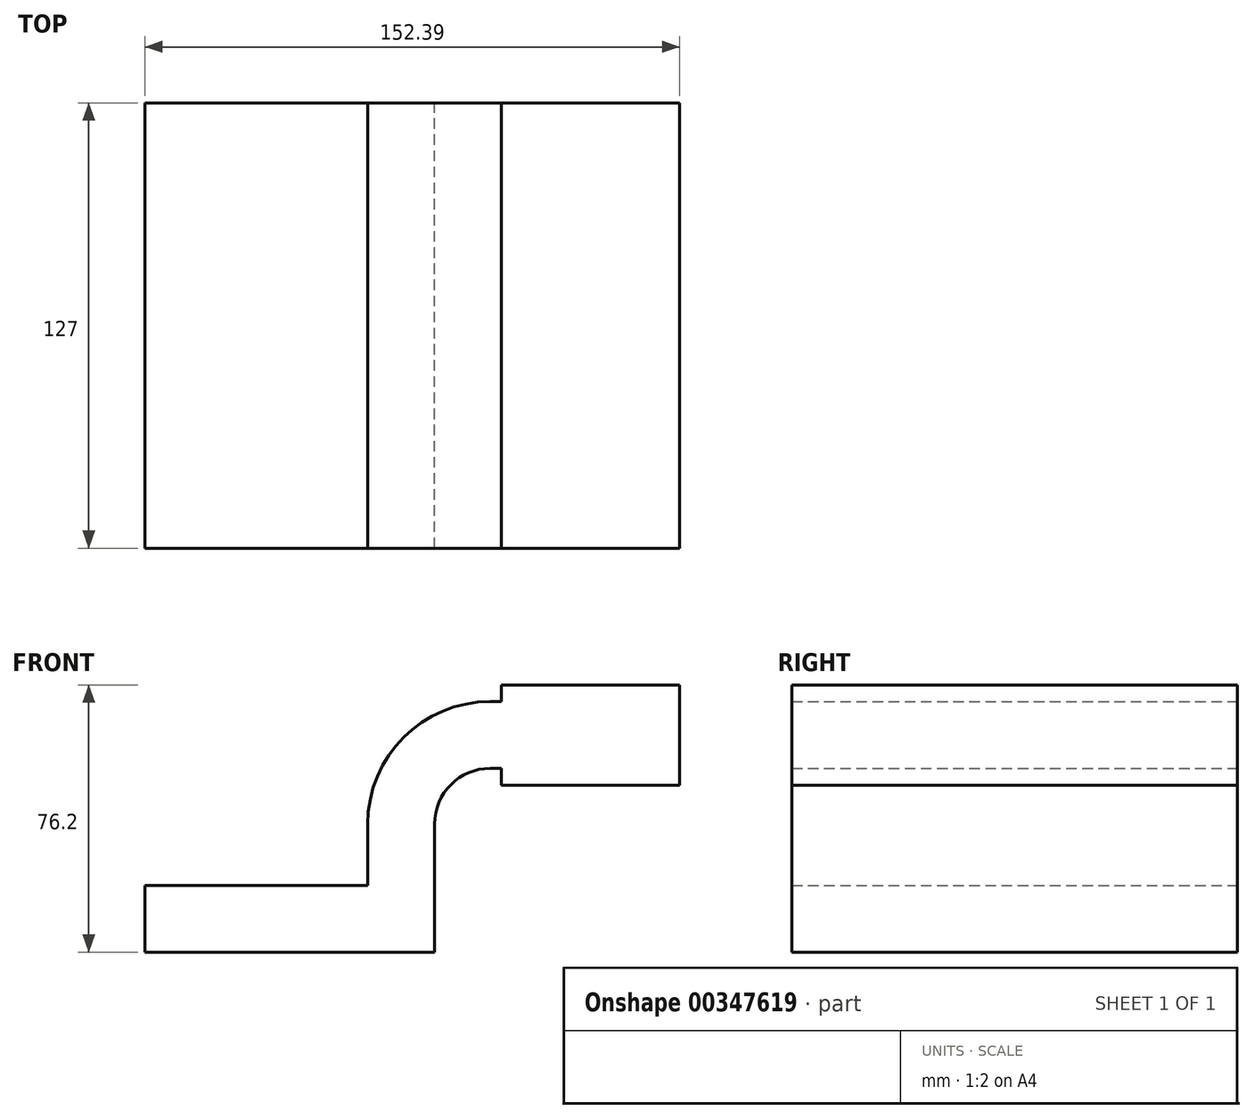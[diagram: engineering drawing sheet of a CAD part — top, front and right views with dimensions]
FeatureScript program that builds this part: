
annotation { "Feature Type Name" : "Feature", "Feature Type Description" : "" }
export const myFeature = defineFeature(function(context is Context, id is Id, definition is map)
    precondition{}
    {
        {
            var Q0;
            Q0=qCreatedBy(makeId("Front.planeOp"),FACE);
            var sketch = newSketch(context, id + "F0", { "sketchPlane" : qUnion([Q0])});
            skLineSegment(sketch, "E0.bottom", {"start": v(41.27, 9.53) * mm, "end": v(-41.28, 9.53) * mm});
            skLineSegment(sketch, "E0.top", {"start": v(41.28, -9.52) * mm, "end": v(-41.27, -9.52) * mm});
            skLineSegment(sketch, "E0.left", {"start": v(41.28, 9.53) * mm, "end": v(41.28, -9.52) * mm});
            skLineSegment(sketch, "E0.right", {"start": v(-41.28, 9.53) * mm, "end": v(-41.27, -9.52) * mm});
            skPoint(sketch, "E0.middle", {"position": v(0, 0) * mm});
            skLineSegment(sketch, "E1.bottom", {"start": v(111.12, 38.1) * mm, "end": v(60.32, 38.1) * mm});
            skLineSegment(sketch, "E1.top", {"start": v(111.12, 66.68) * mm, "end": v(60.32, 66.68) * mm});
            skLineSegment(sketch, "E1.left", {"start": v(111.12, 38.1) * mm, "end": v(111.12, 66.68) * mm});
            skLineSegment(sketch, "E1.right", {"start": v(60.32, 38.1) * mm, "end": v(60.32, 66.68) * mm});
            skPoint(sketch, "E1.middle", {"position": v(85.72, 52.39) * mm});
            skLineSegment(sketch, "E2.bottom", {"start": v(41.27, 27) * mm, "end": v(41.27, 27) * mm});
            skLineSegment(sketch, "E2.top", {"start": v(41.28, -7.95) * mm, "end": v(41.28, -7.95) * mm});
            skLineSegment(sketch, "E2.left", {"start": v(41.27, 27) * mm, "end": v(41.27, -7.95) * mm});
            skLineSegment(sketch, "E2.right", {"start": v(41.27, 27) * mm, "end": v(41.27, -7.95) * mm});
            skPoint(sketch, "E2.middle", {"position": v(41.27, 9.53) * mm});
            skArc(sketch, "E3", {"start": v(41.27, 27) * mm, "mid": v(45.92, 38.23) * mm, "end": v(57.15, 42.88) * mm});
            skLineSegment(sketch, "E4", {"start": v(57.15, 42.88) * mm, "end": v(85.73, 42.88) * mm});
            skArc(sketch, "E5.0", {"start": v(22.22, 27) * mm, "mid": v(32.45, 51.7) * mm, "end": v(57.15, 61.93) * mm});
            skLineSegment(sketch, "E6", {"start": v(22.22, 27) * mm, "end": v(22.22, 9.53) * mm});
            skLineSegment(sketch, "E7", {"start": v(85.72, 42.88) * mm, "end": v(85.72, 66.68) * mm});
            skLineSegment(sketch, "E8", {"start": v(57.15, 61.93) * mm, "end": v(85.72, 61.93) * mm});
            skArc(sketch, "E9", {"start": v(57.15, 61.93) * mm, "mid": v(1.4, 48) * mm, "end": v(-41.28, 9.53) * mm});
            skSolve(sketch);
        }
        {
            var Q0;
            Q0=makeQuery(id+"F0.imprint","IMPRINT",FACE,{"disambiguationData":[TD([[makeQuery(id+"F0.imprint","IMPRINT",EDGE,{"derivedFrom":sQuery(id+"F0.wireOp",EDGE,"E0.top")}),-1.0]])]});
            var Q1;
            Q1=makeQuery(id+"F0.imprint","IMPRINT",FACE,{"disambiguationData":[TD([[makeQuery(id+"F0.imprint","IMPRINT",EDGE,{"derivedFrom":sQuery(id+"F0.wireOp",EDGE,"E5.0")}),1.0]])]});
            var Q2;
            {var subQ0=sQuery(id+"F0.wireOp",EDGE,"E3");Q2=makeQuery(id+"F0.imprint","IMPRINT",FACE,{"disambiguationData":[TD([[makeQuery(id+"F0.imprint","IMPRINT",EDGE,{"derivedFrom":subQ0}),1.0]])]});}
            var Q3;
            {var subQ0=sQuery(id+"F0.wireOp",EDGE,"E4");var subQ1=sQuery(id+"F0.wireOp",EDGE,"E1.right");var subQ2=makeQuery(id+"F0.imprint","INTERSECT",VERTEX,{"derivedFrom":[subQ1,subQ0]});Q3=makeQuery(id+"F0.imprint","IMPRINT",FACE,{"disambiguationData":[TD([[makeQuery(id+"F0.imprint","IMPRINT",EDGE,{"disambiguationData":[TD([[subQ2,-1.0]])],"derivedFrom":subQ1}),-1.0]])]});}
            var Q4;
            {var subQ1=sQuery(id+"F0.wireOp",EDGE,"E1.bottom");Q4=makeQuery(id+"F0.imprint","IMPRINT",FACE,{"disambiguationData":[TD([[makeQuery(id+"F0.imprint","IMPRINT",EDGE,{"derivedFrom":subQ1}),-1.0]])]});}
            var Q5;
            {var subQ0=sQuery(id+"F0.wireOp",EDGE,"E1.right");var subQ1=sQuery(id+"F0.wireOp",EDGE,"E1.top");var subQ2=makeQuery(id+"F0.imprint","INTERSECT",VERTEX,{"derivedFrom":[subQ1,subQ0]});Q5=makeQuery(id+"F0.imprint","IMPRINT",FACE,{"disambiguationData":[TD([[makeQuery(id+"F0.imprint","IMPRINT",EDGE,{"disambiguationData":[TD([[subQ2,1.0]])],"derivedFrom":subQ1}),1.0]])]});}
            extrude(context, id + "F1", {"entities" : qUnion([Q0, Q1, Q2, Q3, Q4, Q5]), "depth" : 127 * mm});
        }
    });
